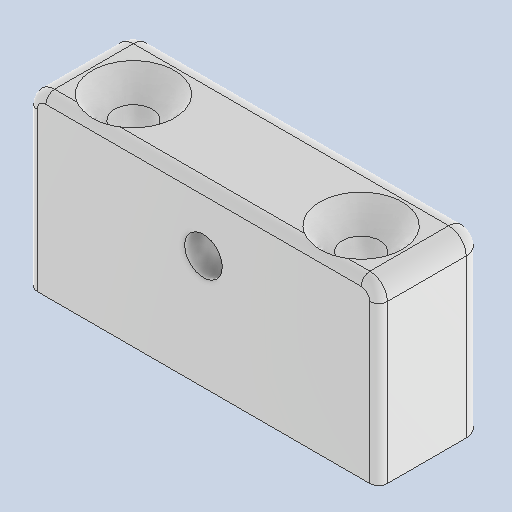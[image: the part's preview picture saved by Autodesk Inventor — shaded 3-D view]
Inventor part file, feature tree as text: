
AUTODESK INVENTOR PART (.ipt)
format: ipt  version: 2025 (Build 290162010, 162A)  size: 196,096 bytes
history: native  units: mm
features: sketch x3, hole x2, fillet x2, extrude x1
ambient origin geometry x8: Origin, YZ Plane, XZ Plane, XY Plane, X Axis, Y Axis, Z Axis, Center Point
bodies: Volumenkörper1 (feature_tree)
feature tree (8):
  extrude  "Extrusion1"  Depth=12.0mm
  hole  "Bohrung1"  [1 undecoded]
  hole  "Bohrung5"  [1 undecoded]
  fillet  "Rundung3"  Radius=7.0mm
  fillet  "Rundung4"  Radius=2.0mm
  sketch  "Skizze1"  dims[d0=40.0mm d1=12.0mm]
  sketch  "Skizze2"  dims[d2=20.0mm d3=0.0mm d4=7.0mm]
  sketch  "Skizze4"  dims[d5=4.3mm d6=6.0mm d7=9.4mm d8=4.0mm d9=90.0deg d10=15.0mm d11=20.594885mm d12=7.0mm d37=7.0mm d38=4.3mm d39=8.0mm d40=9.4mm d41=2.0mm d42=90.0deg d43=10.0mm d44=20.594885mm d45=2.0mm d46=1.0mm d29=1.0mm d30=1.0mm d31=1.0mm d32=0.15mm d33=0.25mm d34=0.375mm d35=14.3117mm d36=0.75mm]
note: 2 required parameter values undecoded (feature->parameter linkage not recoverable at this tier; creation-order binding heuristic only, values carry confidence <= 0.55)
